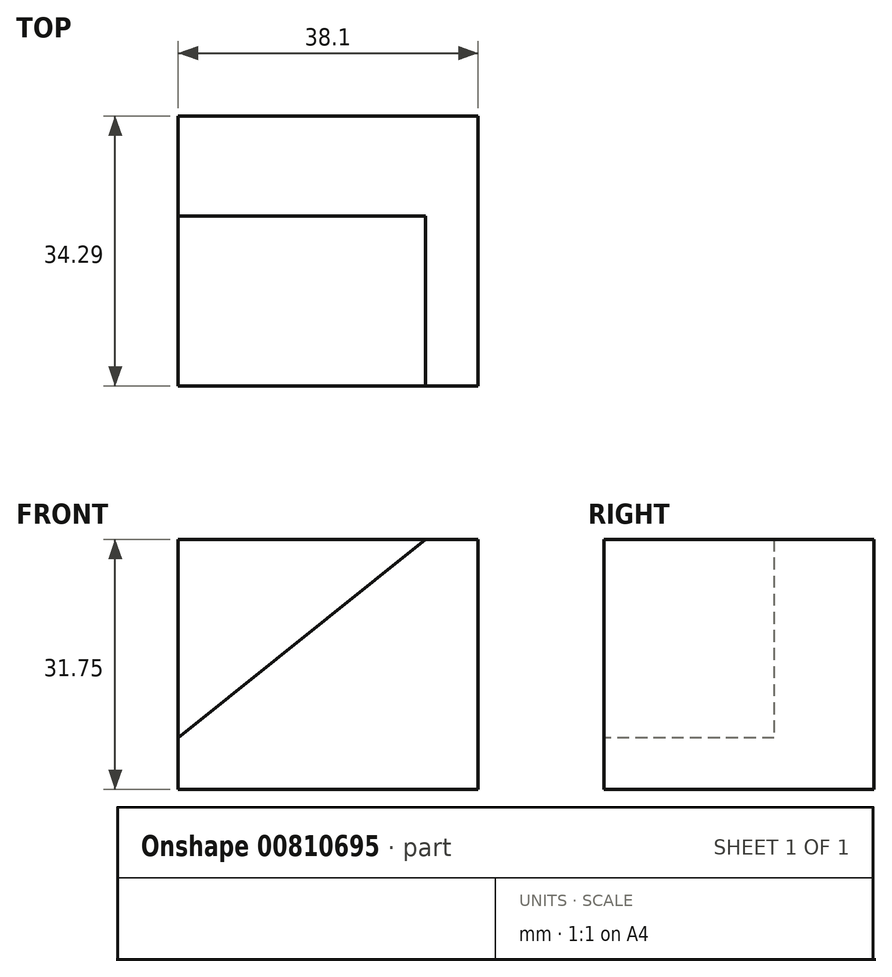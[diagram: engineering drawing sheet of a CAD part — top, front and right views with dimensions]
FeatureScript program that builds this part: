
annotation { "Feature Type Name" : "Feature", "Feature Type Description" : "" }
export const myFeature = defineFeature(function(context is Context, id is Id, definition is map)
    precondition{}
    {
        {
            var Q0;
            Q0=qCreatedBy(makeId("Top.planeOp"),FACE);
            var sketch = newSketch(context, id + "F0", { "sketchPlane" : qUnion([Q0])});
            skLineSegment(sketch, "E0.bottom", {"start": v(0, 0) * mm, "end": v(38.1, 0) * mm});
            skLineSegment(sketch, "E0.top", {"start": v(0, 25.4) * mm, "end": v(38.1, 25.4) * mm});
            skLineSegment(sketch, "E0.left", {"start": v(0, 0) * mm, "end": v(0, 25.4) * mm});
            skLineSegment(sketch, "E0.right", {"start": v(38.1, 0) * mm, "end": v(38.1, 25.4) * mm});
            skSolve(sketch);
        }
        {
            var Q0;
            Q0=qCreatedBy(makeId("Front.planeOp"),FACE);
            var sketch = newSketch(context, id + "F1", { "sketchPlane" : qUnion([Q0])});
            skSolve(sketch);
        }
        {
            var Q0;
            Q0 = qSketchRegion(id + "F1", true);
            var Q1;
            Q1 = qSketchRegion(id + "F0", true);
            extrude(context, id + "F2", {"entities" : qUnion([Q0, Q1]), "depth" : 31.75 * mm, "offsetDistance" : 25.4 * mm});
        }
        {
            var Q0;
            Q0=makeQuery(id+"F2.opExtrude","SWEPT_FACE",FACE,{"disambiguationData":[OSD([sQuery(id+"F0.wireOp",EDGE,"E0.bottom")])]});
            var sketch = newSketch(context, id + "F3", { "sketchPlane" : qUnion([Q0])});
            skLineSegment(sketch, "E1", {"start": v(0, 0) * mm, "end": v(0, 6.52) * mm});
            skLineSegment(sketch, "E2", {"start": v(38.1, 31.75) * mm, "end": v(31.44, 31.75) * mm});
            skLineSegment(sketch, "E3", {"start": v(0, 6.52) * mm, "end": v(31.44, 31.75) * mm});
            skSolve(sketch);
        }
        {
            var Q0;
            {var subQ0=sQuery(id+"F3.wireOp",EDGE,"E3");Q0=makeQuery(id+"F3.imprint","IMPRINT",FACE,{"disambiguationData":[TD([[makeQuery(id+"F3.imprint","IMPRINT",EDGE,{"derivedFrom":subQ0}),1.0]])]});}
            extrude(context, id + "F4", {"entities" : qUnion([Q0]), "operationType" : NewBodyOperationType.REMOVE, "oppositeDirection" : true, "depth" : 12.7 * mm, "offsetDistance" : 25.4 * mm});
        }
        {
            var Q0;
            Q0=makeQuery(id+"F2.opExtrude","SWEPT_FACE",FACE,{"disambiguationData":[OSD([sQuery(id+"F0.wireOp",EDGE,"E0.bottom")])]});
            extrude(context, id + "F5", {"entities" : qUnion([Q0]), "operationType" : NewBodyOperationType.ADD, "depth" : 8.9 * mm, "offsetDistance" : 25.4 * mm});
        }
    });
